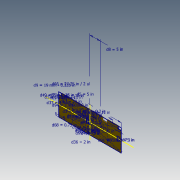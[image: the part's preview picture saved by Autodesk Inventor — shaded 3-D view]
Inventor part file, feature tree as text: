
AUTODESK INVENTOR PART (.ipt)
format: ipt  version: 2020.3 (Build 243373000, 373)  size: 272,384 bytes
history: native  units: in
note: dims shown in document units (in); Inventor stores cm internally (conversion verified against a paired STEP export)
features: hole x5, extrude x4, sketch x3, fillet x3, thread x2, pattern_linear x1, mirror x1
ambient origin geometry x8: Origin, YZ Plane, XZ Plane, XY Plane, X Axis, Y Axis, Z Axis, Center Point
bodies: Solid1 (feature_tree)
feature tree (19):
  sketch  "Sketch1"  dims[d0=30.0in d1=10.5in]
  extrude  "Extrusion1"  Depth=10.5in
  hole  "Hole1"  [1 undecoded]
  thread  "Thread1"  [1 undecoded]
  thread  "Thread2"  [1 undecoded]
  hole  "Hole2"  [1 undecoded]
  fillet  "Fillet1"  Radius=0.413in
  hole  "Hole3"  [1 undecoded]
  hole  "Hole4"  [1 undecoded]
  pattern_linear  "Rectangular Pattern1"  Spacing1=1.0in  [1 undecoded]
  hole  "Hole5"  [1 undecoded]
  fillet  "Fillet2"  Radius=17.0in
  extrude  "Extrusion2"  Depth=0.125in
  extrude  "Extrusion3"  Depth=0.125in
  extrude  "Extrusion4"  Depth=0.125in
  mirror  "Mirror2"
  fillet  "Fillet3"  Radius=2.0in
  sketch  "Sketch3"  dims[d2=1.73in d3=1.02in d4=1.26in d5=5.0in]
  sketch  "Sketch4"  dims[d7=1.26in d8=5.0in d9=0.413in d14=0.23in d15=0.0in d16=0.123in d17=0.75in d18=0.375in d19=0.25in d20=0.5635in d21=1.0in d22=0.8108in d23=1.0in d24=0.0in d25=1.0in d26=0.0in d27=0.265in d28=0.75in d29=0.375in d30=0.25in d31=0.5635in d32=1.0in d33=0.8108in d34=0.375in d35=17.0in d36=2.0in d37=1.5in d38=2.0in d39=2.0in d40=2.0in d41=2.0in d42=0.123in d43=0.75in d44=0.375in d45=0.25in d46=0.5635in d47=1.0in d48=0.8108in d49=3.0in d50=3.0in d51=1.35in d52=0.0in d53=10.0in d54=1.0in d55=0.123in d56=0.75in d57=0.375in d58=0.25in d59=0.5635in d60=1.0in d61=0.8108in d62=0.7874in d64=20.0in d65=1.25in d66=13.625in d67=29.0in d68=0.75in d69=0.75in d70=0.276in d71=0.75in d72=0.433in d73=0.236in d74=90.0deg d75=1.0in d76=0.8108in d77=0.125in d78=2.2in d80=1.4in d81=0.0in d82=0.0in d83=7.261in d84=11.0in d85=11.0in d86=0.2in d87=1.125in d88=1.875in d89=0.0in d90=1.125in d91=13.5in d92=0.0in d93=0.0in d94=3.98in d95=6.25in d96=1.0in d97=0.09in d98=0.6in d99=0.75in d101=0.0in d102=0.0in d104=0.3in d105=0.125in d106=2.0in d107=2.0in]
note: 8 required parameter values undecoded (feature->parameter linkage not recoverable at this tier; creation-order binding heuristic only, values carry confidence <= 0.55)
